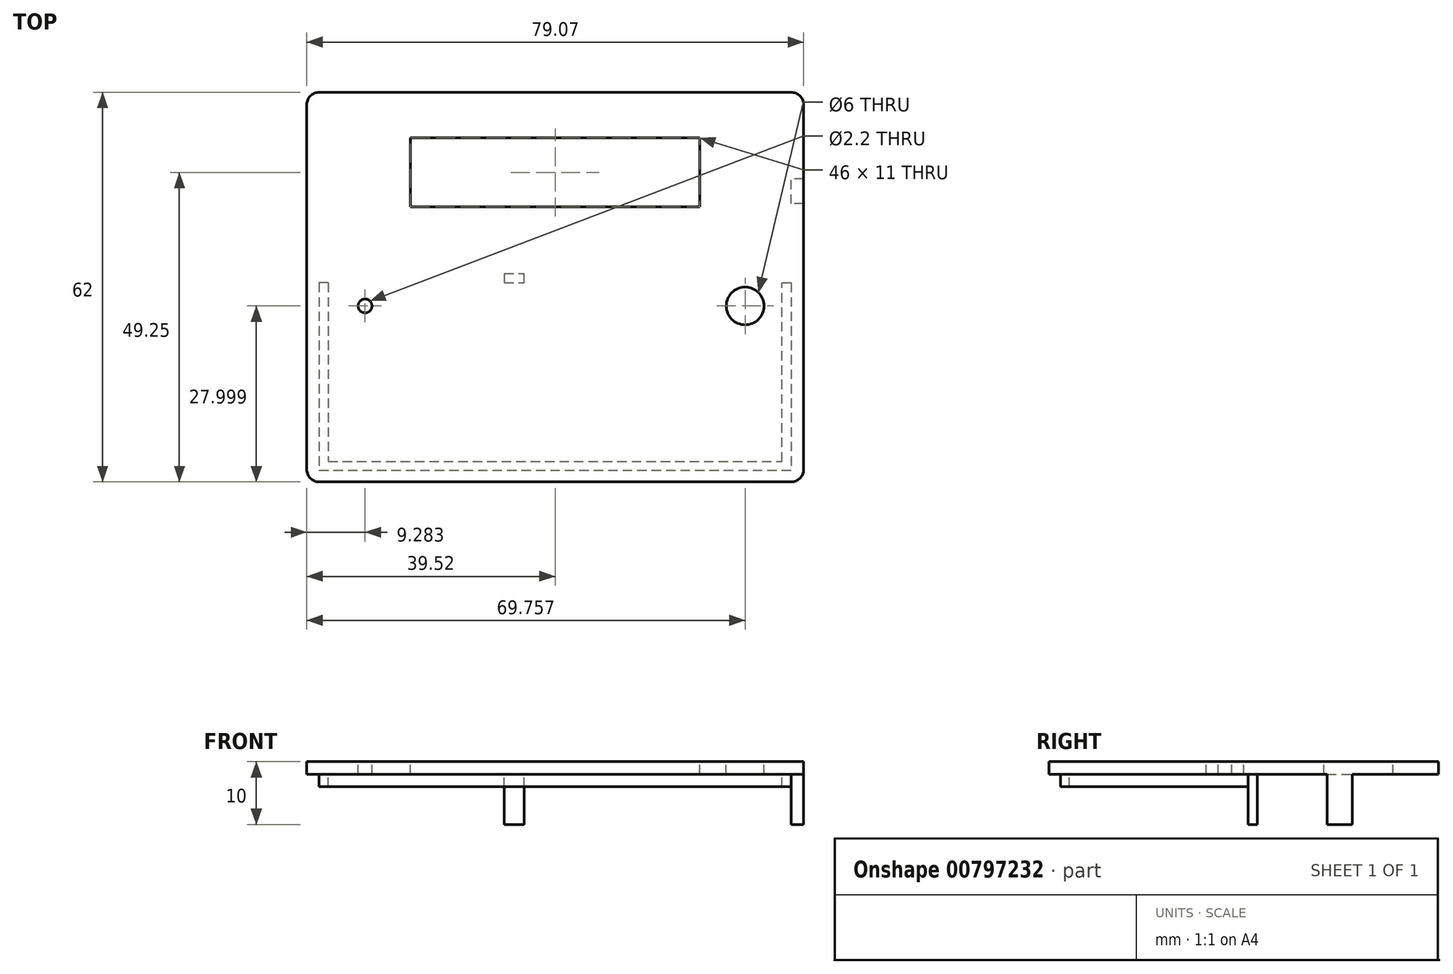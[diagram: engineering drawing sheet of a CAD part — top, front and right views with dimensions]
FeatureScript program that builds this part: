
annotation { "Feature Type Name" : "Feature", "Feature Type Description" : "" }
export const myFeature = defineFeature(function(context is Context, id is Id, definition is map)
    precondition{}
    {
        {
            var Q0;
            Q0=qCreatedBy(makeId("Top.planeOp"),FACE);
            var sketch = newSketch(context, id + "F0", { "sketchPlane" : qUnion([Q0])});
            skPoint(sketch, "E0.middle", {"position": v(0, 0) * mm});
            skLineSegment(sketch, "E1.bottom", {"start": v(36.1, -12.1) * mm, "end": v(-36.1, -12.1) * mm});
            skLineSegment(sketch, "E1.top", {"start": v(36.1, 12.1) * mm, "end": v(-36.1, 12.1) * mm});
            skLineSegment(sketch, "E1.left", {"start": v(36.1, -12.1) * mm, "end": v(36.1, 12.1) * mm});
            skLineSegment(sketch, "E1.right", {"start": v(-36.1, -12.1) * mm, "end": v(-36.1, 12.1) * mm});
            skLineSegment(sketch, "E2", {"start": v(-36.1, 12.1) * mm, "end": v(-25.6, 12.1) * mm});
            skLineSegment(sketch, "E3", {"start": v(-25.6, 12.1) * mm, "end": v(-25.6, 1.6) * mm});
            skLineSegment(sketch, "E4", {"start": v(36.1, 12.1) * mm, "end": v(29.1, 12.1) * mm});
            skLineSegment(sketch, "E5", {"start": v(29.1, 12.1) * mm, "end": v(29.1, 2.1) * mm});
            skLineSegment(sketch, "E6", {"start": v(-37.55, -12.1) * mm, "end": v(-37.55, 13.53) * mm});
            skLineSegment(sketch, "E7", {"start": v(37.55, -2) * mm, "end": v(37.55, 13.53) * mm});
            skLineSegment(sketch, "E8.bottom", {"start": v(-39.55, 15.75) * mm, "end": v(39.55, 15.75) * mm});
            skCircle(sketch, "E9", {"center": v(-25.6, 1.6) * mm, "radius": 3 * mm});
            skCircle(sketch, "E10", {"center": v(29.1, 2.1) * mm, "radius": 3 * mm});
            skCircle(sketch, "E11", {"center": v(-25.6, 1.6) * mm, "radius": 1.1 * mm});
            skCircle(sketch, "E12", {"center": v(29.1, 2.1) * mm, "radius": 1.1 * mm});
            skLineSegment(sketch, "E13", {"start": v(-25.6, 1.6) * mm, "end": v(-22.6, 1.6) * mm});
            skLineSegment(sketch, "E14", {"start": v(39.55, 0) * mm, "end": v(39.55, -2) * mm});
            skLineSegment(sketch, "E15", {"start": v(39.55, 0) * mm, "end": v(39.55, 2) * mm});
            skLineSegment(sketch, "E16", {"start": v(39.55, 2) * mm, "end": v(37.55, 2) * mm});
            skLineSegment(sketch, "E17", {"start": v(39.55, -2) * mm, "end": v(37.55, -2) * mm});
            skLineSegment(sketch, "E18", {"start": v(-36.1, -14.56) * mm, "end": v(36.1, -14.56) * mm});
            skLineSegment(sketch, "E19", {"start": v(-37.55, 13.53) * mm, "end": v(37.55, 13.53) * mm});
            skLineSegment(sketch, "E20", {"start": v(36.1, -43) * mm, "end": v(36.1, -14.56) * mm});
            skLineSegment(sketch, "E21.bottom", {"start": v(39.55, 15.75) * mm, "end": v(-39.52, 15.75) * mm});
            skLineSegment(sketch, "E21.left", {"start": v(39.55, 15.75) * mm, "end": v(39.55, -46.25) * mm});
            skLineSegment(sketch, "E21.right", {"start": v(-39.52, 15.75) * mm, "end": v(-39.52, -46.25) * mm});
            skLineSegment(sketch, "E22.top", {"start": v(-37.55, -44.4) * mm, "end": v(37.55, -44.4) * mm});
            skLineSegment(sketch, "E22.left", {"start": v(-37.55, 13.53) * mm, "end": v(-37.55, -12.1) * mm});
            skLineSegment(sketch, "E22.right", {"start": v(37.55, 13.53) * mm, "end": v(37.55, -2) * mm});
            skLineSegment(sketch, "E23.bottom", {"start": v(-36.1, 12.1) * mm, "end": v(36.1, 12.1) * mm});
            skLineSegment(sketch, "E23.top", {"start": v(-36.1, -43) * mm, "end": v(36.1, -43) * mm});
            skLineSegment(sketch, "E23.left", {"start": v(-36.1, 12.1) * mm, "end": v(-36.1, -12.1) * mm});
            skLineSegment(sketch, "E23.right", {"start": v(36.1, 12.1) * mm, "end": v(36.1, -12.1) * mm});
            skLineSegment(sketch, "E24", {"start": v(-39.52, -46.25) * mm, "end": v(39.55, -46.25) * mm});
            skLineSegment(sketch, "E25", {"start": v(36.1, -14.56) * mm, "end": v(37.55, -14.56) * mm});
            skLineSegment(sketch, "E26", {"start": v(-36.1, -14.56) * mm, "end": v(-37.55, -14.56) * mm});
            skLineSegment(sketch, "E27.trimOffspring", {"start": v(-36.1, -14.56) * mm, "end": v(-36.1, -43) * mm});
            skLineSegment(sketch, "E28.trimOffspring", {"start": v(-37.55, -14.56) * mm, "end": v(-37.55, -44.4) * mm});
            skLineSegment(sketch, "E29.trimOffspring", {"start": v(36.1, -14.56) * mm, "end": v(36.1, -43) * mm});
            skLineSegment(sketch, "E30.trimOffspring", {"start": v(37.55, -14.56) * mm, "end": v(37.55, -44.4) * mm});
            skLineSegment(sketch, "E31", {"start": v(-8.1, -13.07) * mm, "end": v(-8.1, -14.56) * mm});
            skLineSegment(sketch, "E32", {"start": v(-4.93, -14.56) * mm, "end": v(-4.93, -13.07) * mm});
            skCircle(sketch, "E33", {"center": v(-30.24, -18.25) * mm, "radius": 1.1 * mm});
            skCircle(sketch, "E34", {"center": v(-30.24, -18.25) * mm, "radius": 3 * mm});
            skLineSegment(sketch, "E35", {"start": v(0, 0) * mm, "end": v(0, 7.6) * mm});
            skCircle(sketch, "E36.MirrorC", {"center": v(30.24, -18.25) * mm, "radius": 3 * mm});
            skCircle(sketch, "E37.MirrorC", {"center": v(30.24, -18.25) * mm, "radius": 1.1 * mm});
            skLineSegment(sketch, "E38", {"start": v(-37.55, 13.53) * mm, "end": v(-37.55, -13.07) * mm});
            skLineSegment(sketch, "E39", {"start": v(-37.55, -13.07) * mm, "end": v(37.55, -13.07) * mm});
            skLineSegment(sketch, "E40", {"start": v(37.55, -13.07) * mm, "end": v(37.55, -2) * mm});
            skLineSegment(sketch, "E41", {"start": v(0, 0) * mm, "end": v(0, 8.5) * mm});
            skLineSegment(sketch, "E42", {"start": v(23, 8.5) * mm, "end": v(23, -2.5) * mm});
            skLineSegment(sketch, "E43", {"start": v(23, -2.5) * mm, "end": v(-23, -2.5) * mm});
            skLineSegment(sketch, "E44", {"start": v(-23, -2.5) * mm, "end": v(-23, 8.5) * mm});
            skLineSegment(sketch, "E45", {"start": v(-23, 8.5) * mm, "end": v(23, 8.5) * mm});
            skSolve(sketch);
        }
        {
            var Q0;
            {var subQ10=sQuery(id+"F0.wireOp",EDGE,"E16");Q0=makeQuery(id+"F0.imprint","IMPRINT",FACE,{"disambiguationData":[TD([[makeQuery(id+"F0.imprint","IMPRINT",EDGE,{"derivedFrom":subQ10}),-1.0]])]});}
            extrude(context, id + "F1", {"entities" : qUnion([Q0]), "oppositeDirection" : true, "depth" : 2 * mm, "offsetDistance" : 25 * mm});
        }
        {
            var Q0;
            Q0=makeQuery(id+"F0.imprint","IMPRINT",FACE,{"disambiguationData":[TD([[makeQuery(id+"F0.imprint","IMPRINT",EDGE,{"derivedFrom":sQuery(id+"F0.wireOp",EDGE,"E1.bottom")}),-1.0]])]});
            var Q1;
            Q1=makeQuery(id+"F0.imprint","IMPRINT",FACE,{"disambiguationData":[TD([[makeQuery(id+"F0.imprint","IMPRINT",EDGE,{"derivedFrom":sQuery(id+"F0.wireOp",EDGE,"E1.bottom")}),1.0]])]});
            var Q2;
            {var subQ0=sQuery(id+"F0.wireOp",EDGE,"E13");var subQ1=sQuery(id+"F0.wireOp",EDGE,"E3");var subQ2=makeQuery(id+"F0.imprint","INTERSECT",VERTEX,{"derivedFrom":[subQ1,subQ0]});Q2=makeQuery(id+"F0.imprint","IMPRINT",FACE,{"disambiguationData":[TD([[makeQuery(id+"F0.imprint","IMPRINT",EDGE,{"disambiguationData":[TD([[subQ2,1.0]])],"derivedFrom":subQ1}),-1.0]])]});}
            var Q3;
            {var subQ0=sQuery(id+"F0.wireOp",EDGE,"E13");var subQ1=sQuery(id+"F0.wireOp",EDGE,"E3");var subQ2=makeQuery(id+"F0.imprint","INTERSECT",VERTEX,{"derivedFrom":[subQ1,subQ0]});Q3=makeQuery(id+"F0.imprint","IMPRINT",FACE,{"disambiguationData":[TD([[makeQuery(id+"F0.imprint","IMPRINT",EDGE,{"disambiguationData":[TD([[subQ2,1.0]])],"derivedFrom":subQ1}),1.0]])]});}
            var Q4;
            {var subQ0=sQuery(id+"F0.wireOp",EDGE,"E9");var subQ1=sQuery(id+"F0.wireOp",EDGE,"E3");var subQ2=makeQuery(id+"F0.imprint","INTERSECT",VERTEX,{"derivedFrom":[subQ1,subQ0]});Q4=makeQuery(id+"F0.imprint","IMPRINT",FACE,{"disambiguationData":[TD([[makeQuery(id+"F0.imprint","IMPRINT",EDGE,{"disambiguationData":[TD([[subQ2,-1.0]])],"derivedFrom":subQ1}),1.0]])]});}
            var Q5;
            {var subQ0=sQuery(id+"F0.wireOp",EDGE,"E9");var subQ1=sQuery(id+"F0.wireOp",EDGE,"E3");var subQ2=makeQuery(id+"F0.imprint","INTERSECT",VERTEX,{"derivedFrom":[subQ1,subQ0]});Q5=makeQuery(id+"F0.imprint","IMPRINT",FACE,{"disambiguationData":[TD([[makeQuery(id+"F0.imprint","IMPRINT",EDGE,{"disambiguationData":[TD([[subQ2,-1.0]])],"derivedFrom":subQ1}),-1.0]])]});}
            var Q6;
            Q6=makeQuery(id+"F0.imprint","IMPRINT",FACE,{"disambiguationData":[TD([[makeQuery(id+"F0.imprint","IMPRINT",EDGE,{"derivedFrom":sQuery(id+"F0.wireOp",EDGE,"E10")}),1.0]])]});
            var Q7;
            Q7=makeQuery(id+"F0.imprint","IMPRINT",FACE,{"disambiguationData":[TD([[makeQuery(id+"F0.imprint","IMPRINT",EDGE,{"derivedFrom":sQuery(id+"F0.wireOp",EDGE,"E12")}),1.0]])]});
            var Q8;
            Q8=makeQuery(id+"F0.imprint","IMPRINT",FACE,{"disambiguationData":[TD([[makeQuery(id+"F0.imprint","IMPRINT",EDGE,{"derivedFrom":sQuery(id+"F0.wireOp",EDGE,"E23.top")}),1.0]])]});
            var Q9;
            Q9=makeQuery(id+"F0.imprint","IMPRINT",FACE,{"disambiguationData":[TD([[makeQuery(id+"F0.imprint","IMPRINT",EDGE,{"derivedFrom":sQuery(id+"F0.wireOp",EDGE,"E22.top")}),1.0]])]});
            var Q10;
            Q10=makeQuery(id+"F0.imprint","IMPRINT",FACE,{"disambiguationData":[TD([[makeQuery(id+"F0.imprint","IMPRINT",EDGE,{"derivedFrom":sQuery(id+"F0.wireOp",EDGE,"E36.MirrorC")}),-1.0]])]});
            var Q11;
            Q11=makeQuery(id+"F0.imprint","IMPRINT",FACE,{"disambiguationData":[TD([[makeQuery(id+"F0.imprint","IMPRINT",EDGE,{"derivedFrom":sQuery(id+"F0.wireOp",EDGE,"E33")}),-1.0]])]});
            extrude(context, id + "F2", {"entities" : qUnion([Q0, Q1, Q2, Q3, Q4, Q5, Q6, Q7, Q8, Q9, Q10, Q11]), "operationType" : NewBodyOperationType.ADD, "oppositeDirection" : true, "depth" : 2 * mm, "offsetDistance" : 25 * mm});
        }
        {
            var Q0;
            Q0=makeQuery(id+"F0.imprint","IMPRINT",FACE,{"disambiguationData":[TD([[makeQuery(id+"F0.imprint","IMPRINT",EDGE,{"derivedFrom":sQuery(id+"F0.wireOp",EDGE,"E14")}),-1.0]])]});
            var Q1;
            {var subQ0=sQuery(id+"F0.wireOp",EDGE,"E16");Q1=makeQuery(id+"F0.imprint","IMPRINT",FACE,{"disambiguationData":[TD([[makeQuery(id+"F0.imprint","IMPRINT",EDGE,{"derivedFrom":subQ0}),1.0]])]});}
            var Q2;
            {var subQ0=sQuery(id+"F0.wireOp",EDGE,"E31");Q2=makeQuery(id+"F0.imprint","IMPRINT",FACE,{"disambiguationData":[TD([[makeQuery(id+"F0.imprint","IMPRINT",EDGE,{"derivedFrom":subQ0}),1.0]])]});}
            extrude(context, id + "F3", {"entities" : qUnion([Q0, Q1, Q2]), "operationType" : NewBodyOperationType.ADD, "oppositeDirection" : true, "depth" : 10 * mm, "offsetDistance" : 25 * mm});
        }
        {
            var Q0;
            Q0=makeQuery(id+"F0.imprint","IMPRINT",FACE,{"disambiguationData":[TD([[makeQuery(id+"F0.imprint","IMPRINT",EDGE,{"derivedFrom":sQuery(id+"F0.wireOp",EDGE,"E22.top")}),1.0]])]});
            extrude(context, id + "F4", {"entities" : qUnion([Q0]), "operationType" : NewBodyOperationType.ADD, "oppositeDirection" : true, "depth" : 4 * mm, "offsetDistance" : 25 * mm});
        }
        {
            var Q0;
            Q0=makeQuery(id+"F1.opExtrude","SWEPT_EDGE",EDGE,{"disambiguationData":[OSD([sQuery(id+"F0.wireOp",EDGE,"E21.bottom"),sQuery(id+"F0.wireOp",EDGE,"E21.right")])]});
            var Q1;
            Q1=makeQuery(id+"F1.opExtrude","SWEPT_EDGE",EDGE,{"disambiguationData":[OSD([sQuery(id+"F0.wireOp",EDGE,"E21.bottom"),sQuery(id+"F0.wireOp",EDGE,"E21.left")])]});
            var Q2;
            Q2=makeQuery(id+"F1.opExtrude","SWEPT_EDGE",EDGE,{"disambiguationData":[OSD([sQuery(id+"F0.wireOp",EDGE,"E21.left"),sQuery(id+"F0.wireOp",EDGE,"E24")])]});
            var Q3;
            Q3=makeQuery(id+"F1.opExtrude","SWEPT_EDGE",EDGE,{"disambiguationData":[OSD([sQuery(id+"F0.wireOp",EDGE,"E21.right"),sQuery(id+"F0.wireOp",EDGE,"E24")])]});
            fillet(context, id + "F5", {"entities" : qUnion([Q0, Q1, Q2, Q3]), "radius" : 2 * mm, "tangentPropagation" : true, "allowEdgeOverflow" : false});
        }
    });
